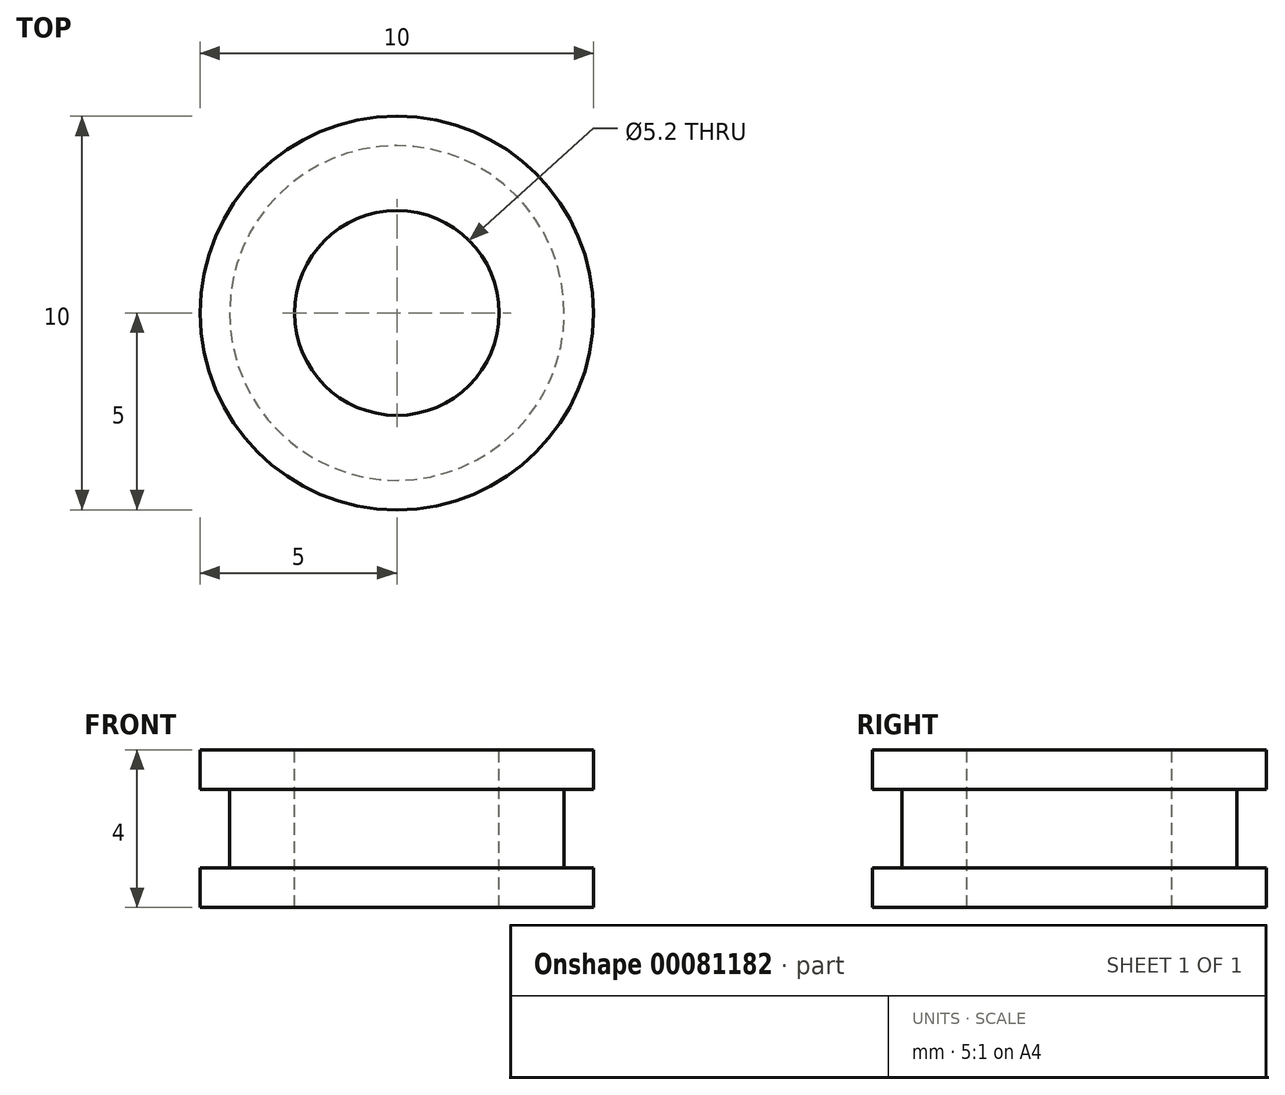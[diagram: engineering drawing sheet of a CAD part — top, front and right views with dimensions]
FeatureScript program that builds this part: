
annotation { "Feature Type Name" : "Feature", "Feature Type Description" : "" }
export const myFeature = defineFeature(function(context is Context, id is Id, definition is map)
    precondition{}
    {
        {
            var Q0;
            Q0=qCreatedBy(makeId("Top.planeOp"),FACE);
            var sketch = newSketch(context, id + "F0", { "sketchPlane" : qUnion([Q0])});
            skCircle(sketch, "E0", {"center": v(0, 0) * mm, "radius": 5 * mm});
            skSolve(sketch);
        }
        {
            var Q0;
            Q0=qSketchRegion(id+"F0",true);
            extrude(context, id + "F1", {"entities" : qUnion([Q0]), "depth" : 4 * mm});
        }
        {
            var Q0;
            Q0=makeQuery(id+"F1.opExtrude","CAP_FACE",FACE,{"disambiguationData":[OSD([sQuery(id+"F0.wireOp",EDGE,"E0")])],"isStart":false});
            var sketch = newSketch(context, id + "F2", { "sketchPlane" : qUnion([Q0])});
            skCircle(sketch, "E1", {"center": v(0, 0) * mm, "radius": 2.6 * mm});
            skSolve(sketch);
        }
        {
            var Q0;
            Q0=makeQuery(id+"F1.opExtrude","CAP_FACE",FACE,{"disambiguationData":[OSD([sQuery(id+"F0.wireOp",EDGE,"E0")])],"isStart":true});
            var sketch = newSketch(context, id + "F3", { "sketchPlane" : qUnion([Q0])});
            skCircle(sketch, "E2", {"center": v(0, 0) * mm, "radius": 4.25 * mm});
            skSolve(sketch);
        }
        {
            var Q0;
            Q0=makeQuery(id+"F3.imprint","IMPRINT",FACE,{"disambiguationData":[TD([[makeQuery(id+"F3.imprint","IMPRINT",EDGE,{"derivedFrom":sQuery(id+"F3.wireOp",EDGE,"E2")}),-1.0]])]});
            extrude(context, id + "F4", {"entities" : qUnion([Q0]), "operationType" : NewBodyOperationType.REMOVE, "oppositeDirection" : true, "depth" : 3 * mm});
        }
        {
            var Q0;
            Q0=makeQuery(id+"F2.imprint","IMPRINT",FACE,{"disambiguationData":[TD([[makeQuery(id+"F2.imprint","IMPRINT",EDGE,{"derivedFrom":sQuery(id+"F2.wireOp",EDGE,"E1")}),1.0]])]});
            extrude(context, id + "F5", {"entities" : qUnion([Q0]), "operationType" : NewBodyOperationType.REMOVE, "endBound" : BoundingType.THROUGH_ALL, "oppositeDirection" : true, "depth" : 25 * mm});
        }
        {
            var Q0;
            Q0=makeQuery(id+"F3.imprint","IMPRINT",FACE,{"disambiguationData":[TD([[makeQuery(id+"F3.imprint","IMPRINT",EDGE,{"derivedFrom":sQuery(id+"F3.wireOp",EDGE,"E2")}),-1.0]])]});
            extrude(context, id + "F6", {"entities" : qUnion([Q0]), "operationType" : NewBodyOperationType.ADD, "oppositeDirection" : true, "depth" : 1 * mm});
        }
    });
